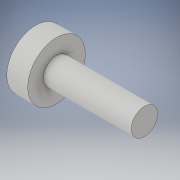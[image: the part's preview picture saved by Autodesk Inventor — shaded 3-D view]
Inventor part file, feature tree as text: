
AUTODESK INVENTOR PART (.ipt)
format: ipt  version: 2018 (Build 220112000, 112)  size: 98,304 bytes
history: native  units: in
note: dims shown in document units (in); Inventor stores cm internally (conversion verified against a paired STEP export)
features: revolve x1, sketch x1
ambient origin geometry x8: Origin, YZ Plane, XZ Plane, XY Plane, X Axis, Y Axis, Z Axis, Center Point
bodies: Solid1 (feature_tree)
feature tree (2):
  revolve  "Revolution1"  [1 undecoded]
  sketch  "Sketch1"  dims[d0=90.0deg]
note: 1 required parameter value undecoded (feature->parameter linkage not recoverable at this tier; creation-order binding heuristic only, values carry confidence <= 0.55)
